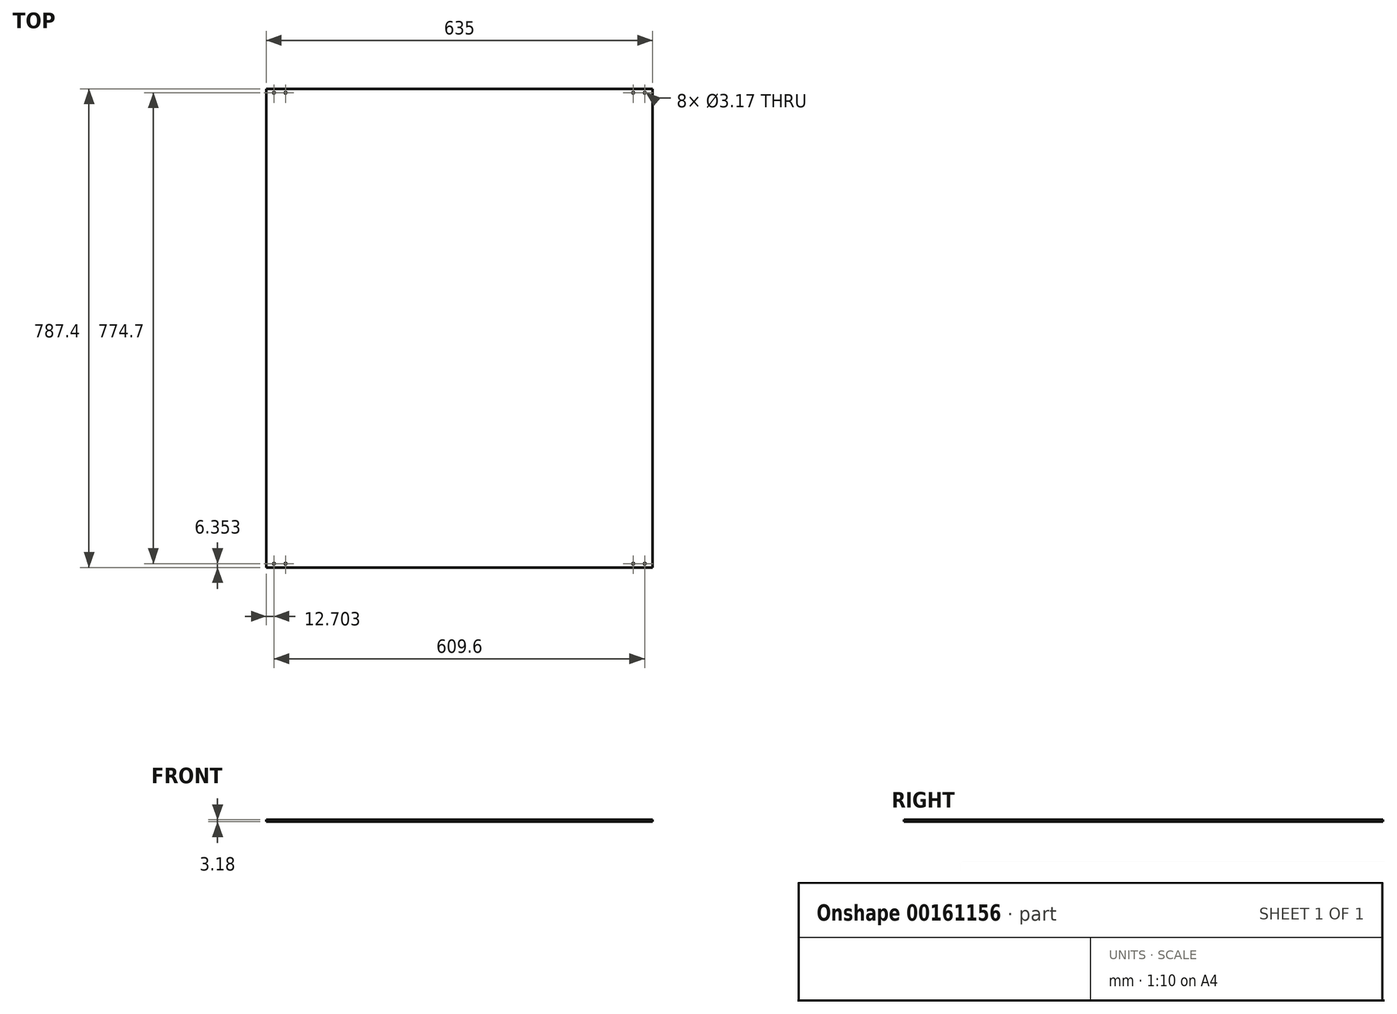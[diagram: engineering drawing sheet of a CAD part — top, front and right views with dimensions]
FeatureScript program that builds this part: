
annotation { "Feature Type Name" : "Feature", "Feature Type Description" : "" }
export const myFeature = defineFeature(function(context is Context, id is Id, definition is map)
    precondition{}
    {
        {
            var Q0;
            Q0=qCreatedBy(makeId("Top.planeOp"),FACE);
            var sketch = newSketch(context, id + "F0", { "sketchPlane" : qUnion([Q0])});
            skLineSegment(sketch, "E0", {"start": v(-336.4, 382.75) * mm, "end": v(298.6, 382.75) * mm});
            skLineSegment(sketch, "E1", {"start": v(298.6, 382.75) * mm, "end": v(298.6, -404.65) * mm});
            skLineSegment(sketch, "E2", {"start": v(298.6, -404.65) * mm, "end": v(-336.4, -404.65) * mm});
            skLineSegment(sketch, "E3", {"start": v(-336.4, -404.65) * mm, "end": v(-336.4, 382.75) * mm});
            skCircle(sketch, "E4", {"center": v(-323.7, -398.3) * mm, "radius": 1.59 * mm});
            skCircle(sketch, "E5", {"center": v(-304.66, -398.3) * mm, "radius": 1.59 * mm});
            skCircle(sketch, "E6", {"center": v(285.9, -398.3) * mm, "radius": 1.59 * mm});
            skCircle(sketch, "E7", {"center": v(266.84, -398.3) * mm, "radius": 1.59 * mm});
            skCircle(sketch, "E8", {"center": v(285.9, 376.4) * mm, "radius": 1.59 * mm});
            skCircle(sketch, "E9", {"center": v(266.84, 376.4) * mm, "radius": 1.59 * mm});
            skCircle(sketch, "E10", {"center": v(-323.7, 376.4) * mm, "radius": 1.59 * mm});
            skCircle(sketch, "E11", {"center": v(-304.66, 376.4) * mm, "radius": 1.59 * mm});
            skSolve(sketch);
        }
        {
            var Q0;
            Q0=makeQuery(id+"F0.imprint","IMPRINT",FACE,{"disambiguationData":[TD([[makeQuery(id+"F0.imprint","IMPRINT",EDGE,{"derivedFrom":sQuery(id+"F0.wireOp",EDGE,"E0")}),-1.0]])]});
            extrude(context, id + "F1", {"entities" : qUnion([Q0]), "oppositeDirection" : true, "depth" : 3.17 * mm});
        }
    });
